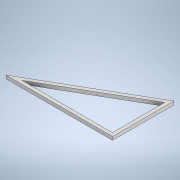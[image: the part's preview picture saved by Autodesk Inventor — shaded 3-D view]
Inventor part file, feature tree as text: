
AUTODESK INVENTOR PART (.ipt)
format: ipt  version: 2021.1 (Build 251245010, 245A)  size: 100,864 bytes
history: native  units: in
note: dims shown in document units (in); Inventor stores cm internally (conversion verified against a paired STEP export)
features: extrude x1, sketch x1
ambient origin geometry x8: Origin, YZ Plane, XZ Plane, XY Plane, X Axis, Y Axis, Z Axis, Center Point
bodies: Solid1 (feature_tree)
feature tree (2):
  extrude  "Extrusion1"  TaperAngle=30.0deg  [1 undecoded]
  sketch  "Sketch1"  dims[d0=8.0in d1=30.0deg d2=0.25in d3=0.25in d4=0.25in d5=0.25in d6=0.0in]
note: 1 required parameter value undecoded (feature->parameter linkage not recoverable at this tier; creation-order binding heuristic only, values carry confidence <= 0.55)
